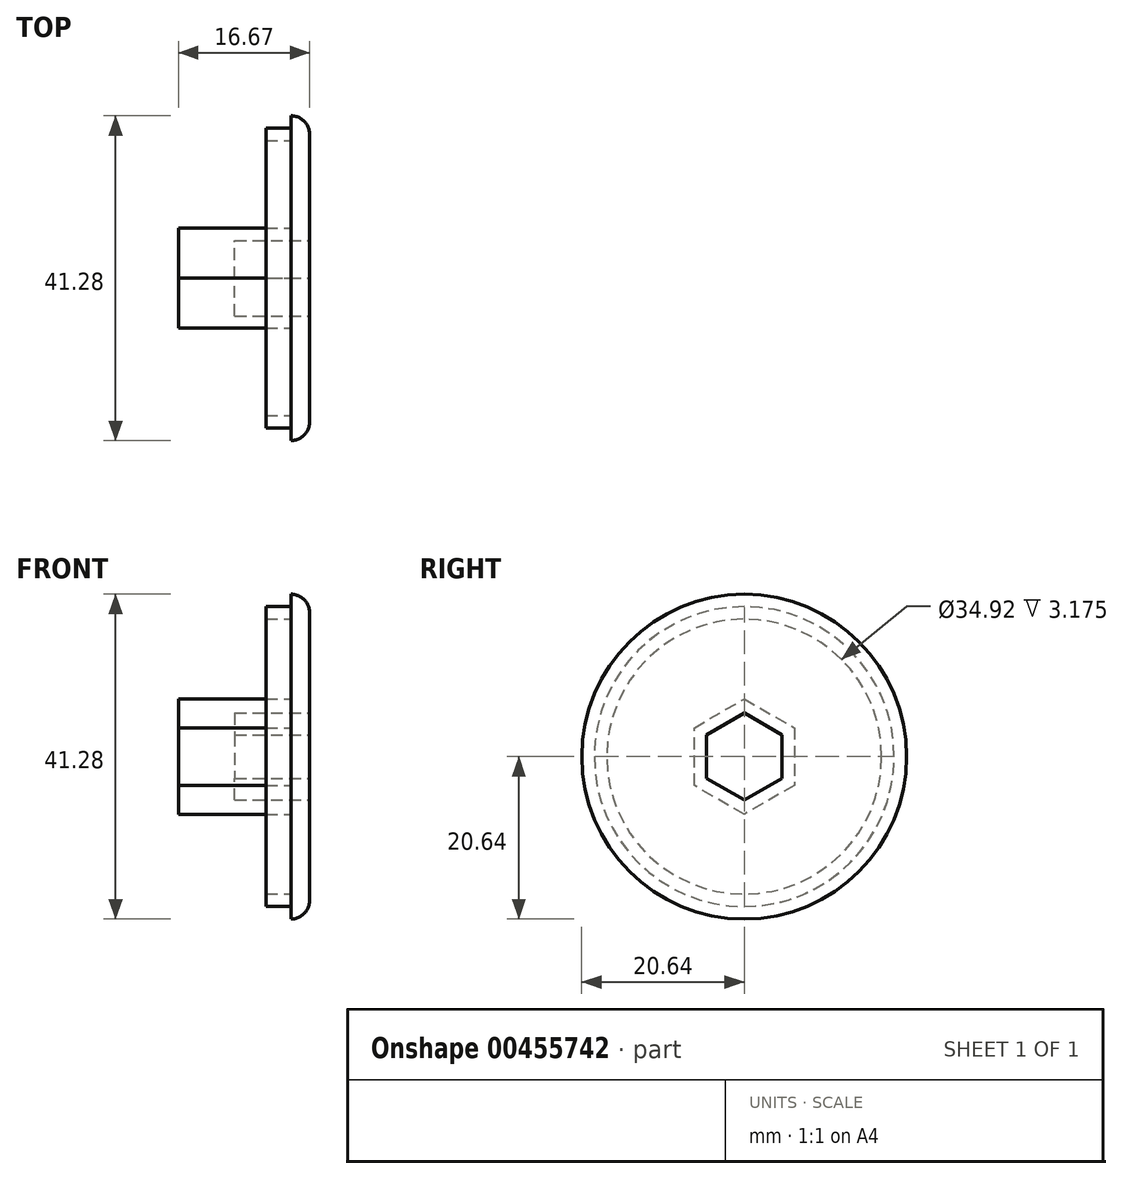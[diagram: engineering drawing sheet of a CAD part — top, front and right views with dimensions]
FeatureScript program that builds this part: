
annotation { "Feature Type Name" : "Feature", "Feature Type Description" : "" }
export const myFeature = defineFeature(function(context is Context, id is Id, definition is map)
    precondition{}
    {
        {
            var Q0;
            Q0=qCreatedBy(makeId("Right.planeOp"),FACE);
            var sketch = newSketch(context, id + "F0", { "sketchPlane" : qUnion([Q0])});
            skCircle(sketch, "E0.cCircle", {"center": v(0, 0) * mm, "radius": 6.35 * mm, "construction": true});
            skLineSegment(sketch, "E0.0", {"start": v(6.35, 3.67) * mm, "end": v(6.35, -3.67) * mm});
            skLineSegment(sketch, "E0.1", {"start": v(6.35, -3.67) * mm, "end": v(0, -7.33) * mm});
            skLineSegment(sketch, "E0.2", {"start": v(0, -7.33) * mm, "end": v(-6.35, -3.67) * mm});
            skLineSegment(sketch, "E0.3", {"start": v(-6.35, -3.67) * mm, "end": v(-6.35, 3.67) * mm});
            skLineSegment(sketch, "E0.4", {"start": v(-6.35, 3.67) * mm, "end": v(0, 7.33) * mm});
            skLineSegment(sketch, "E0.5", {"start": v(0, 7.33) * mm, "end": v(6.35, 3.67) * mm});
            skPoint(sketch, "E0.0.midPoint", {"position": v(6.35, 0) * mm});
            skSolve(sketch);
        }
        {
            var Q0;
            Q0 = qSketchRegion(id + "F0", true);
            extrude(context, id + "F1", {"entities" : qUnion([Q0]), "oppositeDirection" : true, "depth" : 14.29 * mm});
        }
        {
            var Q0;
            Q0=qCreatedBy(makeId("Right.planeOp"),FACE);
            var sketch = newSketch(context, id + "F2", { "sketchPlane" : qUnion([Q0])});
            skCircle(sketch, "E1", {"center": v(0, 0) * mm, "radius": 20.64 * mm});
            skSolve(sketch);
        }
        {
            var Q0;
            Q0 = qSketchRegion(id + "F2", true);
            extrude(context, id + "F3", {"entities" : qUnion([Q0]), "operationType" : NewBodyOperationType.ADD, "depth" : 0.06 * 38.1 * mm});
        }
        {
            var Q0;
            Q0=makeQuery(id+"F3.opExtrude","CAP_FACE",FACE,{"disambiguationData":[OSD([sQuery(id+"F2.wireOp",EDGE,"E1")])],"isStart":false});
            var sketch = newSketch(context, id + "F4", { "sketchPlane" : qUnion([Q0])});
            skCircle(sketch, "E2.cCircle", {"center": v(0, 0) * mm, "radius": 4.79 * mm, "construction": true});
            skLineSegment(sketch, "E2.0", {"start": v(4.79, 2.76) * mm, "end": v(4.79, -2.76) * mm});
            skLineSegment(sketch, "E2.1", {"start": v(4.79, -2.76) * mm, "end": v(0, -5.53) * mm});
            skLineSegment(sketch, "E2.2", {"start": v(0, -5.53) * mm, "end": v(-4.79, -2.76) * mm});
            skLineSegment(sketch, "E2.3", {"start": v(-4.79, -2.76) * mm, "end": v(-4.79, 2.76) * mm});
            skLineSegment(sketch, "E2.4", {"start": v(-4.79, 2.76) * mm, "end": v(0, 5.53) * mm});
            skLineSegment(sketch, "E2.5", {"start": v(0, 5.53) * mm, "end": v(4.79, 2.76) * mm});
            skPoint(sketch, "E2.0.midPoint", {"position": v(4.79, 0) * mm});
            skSolve(sketch);
        }
        {
            var Q0;
            Q0 = qSketchRegion(id + "F4", true);
            extrude(context, id + "F5", {"entities" : qUnion([Q0]), "operationType" : NewBodyOperationType.REMOVE, "oppositeDirection" : true, "depth" : 9.52 * mm});
        }
        {
            var Q0;
            Q0=makeQuery(id+"F3.opExtrude","CAP_FACE",FACE,{"disambiguationData":[OSD([sQuery(id+"F2.wireOp",EDGE,"E1")])],"isStart":true});
            var sketch = newSketch(context, id + "F6", { "sketchPlane" : qUnion([Q0])});
            skCircle(sketch, "E3", {"center": v(0, 0) * mm, "radius": 19.05 * mm});
            skCircle(sketch, "E4.0", {"center": v(0, 0) * mm, "radius": 17.46 * mm});
            skSolve(sketch);
        }
        {
            var Q0;
            Q0 = qSketchRegion(id + "F6", true);
            extrude(context, id + "F7", {"entities" : qUnion([Q0]), "operationType" : NewBodyOperationType.ADD, "depth" : 3.17 * mm});
        }
        {
            var Q0;
            Q0=makeQuery(id+"F3.opExtrude","CAP_EDGE",EDGE,{"disambiguationData":[OSD([sQuery(id+"F2.wireOp",EDGE,"E1")])],"isStart":false});
            fillet(context, id + "F8", {"entities" : qUnion([Q0]), "radius" : 2.38 * mm, "tangentPropagation" : true, "allowEdgeOverflow" : false});
        }
    });
